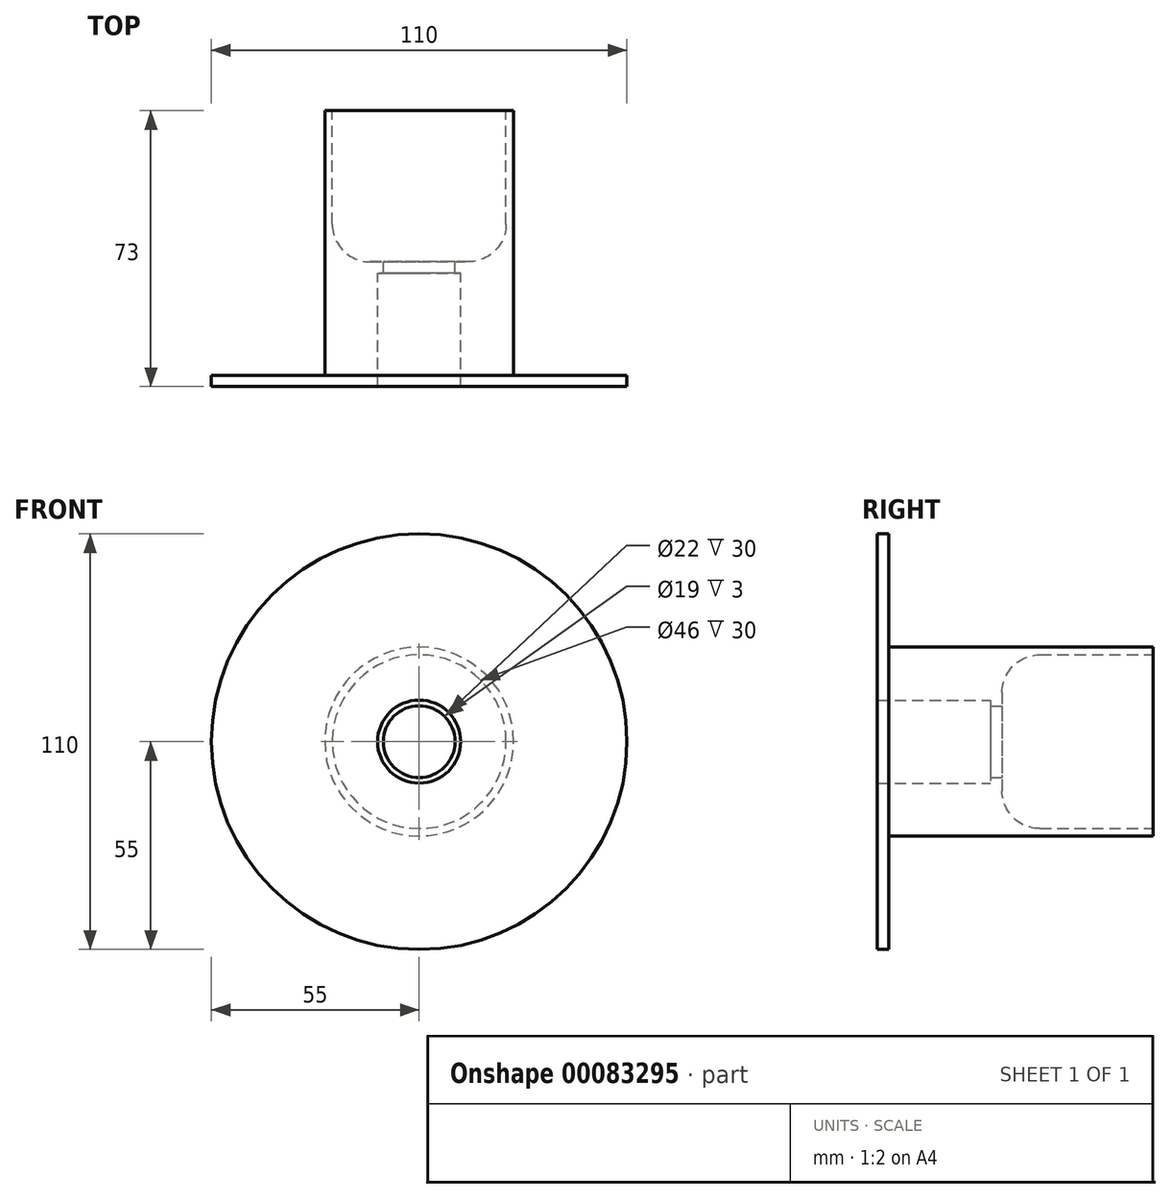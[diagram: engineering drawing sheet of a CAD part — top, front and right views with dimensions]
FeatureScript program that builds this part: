
annotation { "Feature Type Name" : "Feature", "Feature Type Description" : "" }
export const myFeature = defineFeature(function(context is Context, id is Id, definition is map)
    precondition{}
    {
        {
            var Q0;
            Q0=qCreatedBy(makeId("Top.planeOp"),FACE);
            var sketch = newSketch(context, id + "F0", { "sketchPlane" : qUnion([Q0])});
            skLineSegment(sketch, "E0", {"start": v(0, 0) * mm, "end": v(0, 46.62) * mm, "construction": true});
            skLineSegment(sketch, "E1", {"start": v(11, 0) * mm, "end": v(11, 30) * mm});
            skLineSegment(sketch, "E2", {"start": v(11, 30) * mm, "end": v(9.5, 30) * mm});
            skLineSegment(sketch, "E3", {"start": v(9.5, 30) * mm, "end": v(9.5, 33) * mm});
            skLineSegment(sketch, "E4", {"start": v(9.5, 33) * mm, "end": v(23, 33) * mm});
            skLineSegment(sketch, "E5", {"start": v(23, 33) * mm, "end": v(23, 73) * mm});
            skLineSegment(sketch, "E6", {"start": v(23, 73) * mm, "end": v(25, 73) * mm});
            skLineSegment(sketch, "E7", {"start": v(25, 73) * mm, "end": v(25, 3) * mm});
            skLineSegment(sketch, "E8", {"start": v(25, 3) * mm, "end": v(55, 3) * mm});
            skLineSegment(sketch, "E9", {"start": v(55, 3) * mm, "end": v(55, 0) * mm});
            skLineSegment(sketch, "E10", {"start": v(55, 0) * mm, "end": v(11, 0) * mm});
            skSolve(sketch);
        }
        {
            var Q0;
            Q0 = qConstructionFilter(qBodyType(qCreatedBy(id + "F0" ,EDGE), BodyType.WIRE), ConstructionObject.NO);
            var Q1;
            Q1=sQuery(id+"F0.wireOp",EDGE,"E0");
            revolve(context, id + "F1", {"bodyType" : ToolBodyType.SURFACE, "surfaceEntities" : qUnion([Q0]), "axis" : qUnion([Q1]), "revolveType" : RevolveType.FULL});
        }
        {
            var Q0;
            Q0=makeQuery(id+"F1.opRevolve","SWEPT_EDGE",EDGE,{"disambiguationData":[OSD([sQuery(id+"F0.wireOp",VERTEX,"E5.start")])]});
            fillet(context, id + "F2", {"entities" : qUnion([Q0]), "radius" : 10 * mm, "tangentPropagation" : true, "allowEdgeOverflow" : false});
        }
    });
